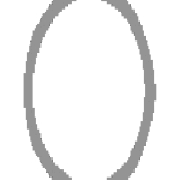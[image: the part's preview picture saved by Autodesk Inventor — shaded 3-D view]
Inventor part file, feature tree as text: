
AUTODESK INVENTOR PART (.ipt)
format: ipt  version: 2021 (Build 250183000, 183)  size: 109,056 bytes
history: native  units: in
note: dims shown in document units (in); Inventor stores cm internally (conversion verified against a paired STEP export)
features: other x4, sketch x3, plane x1
ambient origin geometry x8: Origin, YZ Plane, XZ Plane, XY Plane, X Axis, Y Axis, Z Axis, Center Point
bodies: Solid1 (feature_tree), Body (feature_tree)
feature tree (8):
  other  "Driven Length"
  other  "Frame Generator"
  other  "Start Plane"
  other  "End Plane"
  sketch  "Sketch"  dims[d2=20.2683in d4=-0.0in d5=20.2683in d6=0.12in d7=0.0in d8=90.0deg d9=20.2683in]
  sketch  "Sketch2"  dims[d0=1.0in]
  plane  "Work Plane3"
  sketch  "Sketch3"  dims[d1=0.065in]
